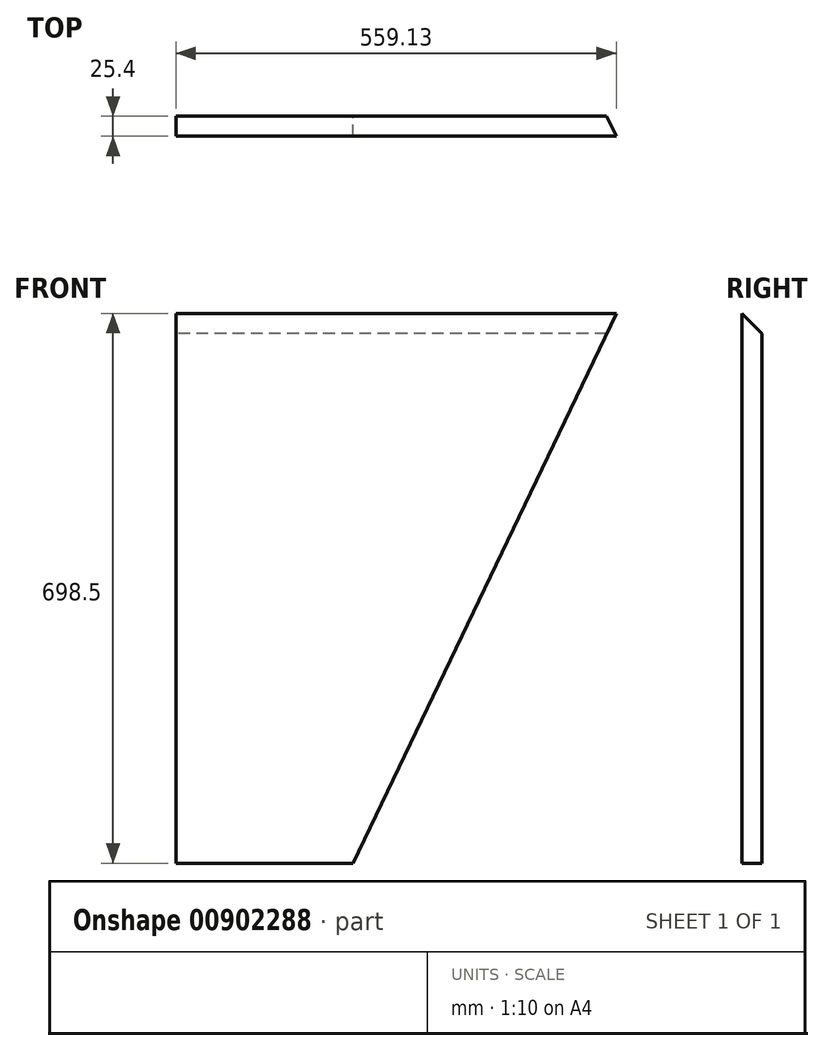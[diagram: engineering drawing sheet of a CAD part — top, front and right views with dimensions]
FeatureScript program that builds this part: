
annotation { "Feature Type Name" : "Feature", "Feature Type Description" : "" }
export const myFeature = defineFeature(function(context is Context, id is Id, definition is map)
    precondition{}
    {
        {
            var Q0;
            Q0=qCreatedBy(makeId("Front.planeOp"),FACE);
            var sketch = newSketch(context, id + "F0", { "sketchPlane" : qUnion([Q0])});
            skLineSegment(sketch, "E0", {"start": v(0, 0) * mm, "end": v(559.13, 0) * mm});
            skLineSegment(sketch, "E1", {"start": v(559.13, 0) * mm, "end": v(224.63, -698.5) * mm});
            skLineSegment(sketch, "E2", {"start": v(224.63, -698.5) * mm, "end": v(0, -698.5) * mm});
            skLineSegment(sketch, "E3", {"start": v(0, -698.5) * mm, "end": v(0, 0) * mm});
            skSolve(sketch);
        }
        {
            var Q0;
            Q0=makeQuery(id+"F0.imprint","IMPRINT",FACE,{"disambiguationData":[TD([[makeQuery(id+"F0.imprint","IMPRINT",EDGE,{"derivedFrom":sQuery(id+"F0.wireOp",EDGE,"E0")}),-1.0]])]});
            extrude(context, id + "F1", {"entities" : qUnion([Q0]), "depth" : 25.4 * mm, "offsetDistance" : 25.4 * mm});
        }
        {
            var Q0;
            Q0=makeQuery(id+"F1.opExtrude","SWEPT_FACE",FACE,{"disambiguationData":[OSD([sQuery(id+"F0.wireOp",EDGE,"E3")])]});
            var sketch = newSketch(context, id + "F2", { "sketchPlane" : qUnion([Q0])});
            skLineSegment(sketch, "E4", {"start": v(25.4, 0) * mm, "end": v(0, -25.4) * mm});
            skSolve(sketch);
        }
        {
            var Q0;
            {var subQ0=sQuery(id+"F2.wireOp",EDGE,"E4");Q0=makeQuery(id+"F2.imprint","IMPRINT",FACE,{"disambiguationData":[TD([[makeQuery(id+"F2.imprint","IMPRINT",EDGE,{"derivedFrom":subQ0}),-1.0]])]});}
            extrude(context, id + "F3", {"entities" : qUnion([Q0]), "operationType" : NewBodyOperationType.REMOVE, "endBound" : BoundingType.THROUGH_ALL, "oppositeDirection" : true, "depth" : 25.4 * mm, "offsetDistance" : 25.4 * mm});
        }
    });
